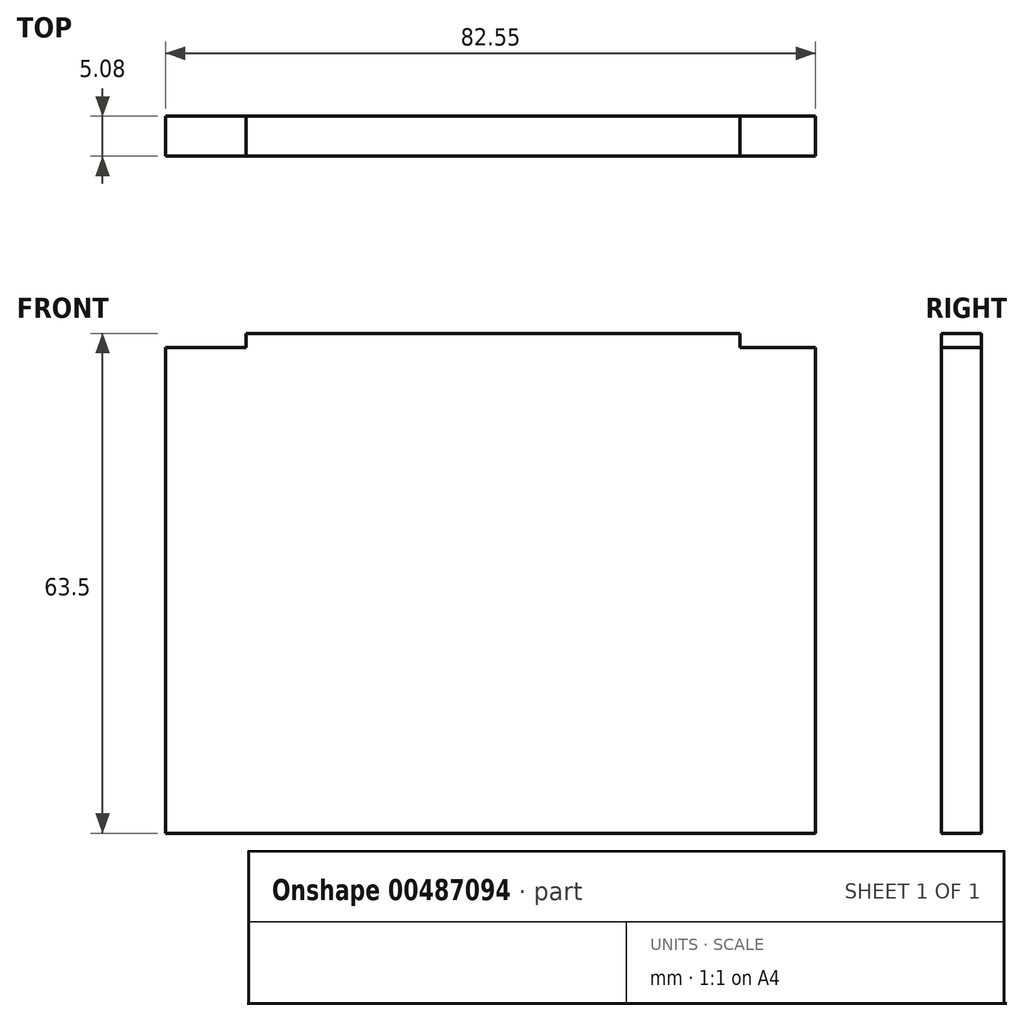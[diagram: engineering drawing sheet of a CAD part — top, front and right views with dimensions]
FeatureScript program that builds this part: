
annotation { "Feature Type Name" : "Feature", "Feature Type Description" : "" }
export const myFeature = defineFeature(function(context is Context, id is Id, definition is map)
    precondition{}
    {
        {
            var Q0;
            Q0=qCreatedBy(makeId("Front.planeOp"),FACE);
            var sketch = newSketch(context, id + "F0", { "sketchPlane" : qUnion([Q0])});
            skLineSegment(sketch, "E0.bottom", {"start": v(-31.37, 30.1) * mm, "end": v(31.37, 30.1) * mm});
            skLineSegment(sketch, "E0.top", {"start": v(-41.58, -33.4) * mm, "end": v(40.97, -33.4) * mm});
            skLineSegment(sketch, "E0.left", {"start": v(-41.58, 28.32) * mm, "end": v(-41.58, -33.4) * mm});
            skLineSegment(sketch, "E0.right", {"start": v(40.97, 28.32) * mm, "end": v(40.97, -33.4) * mm});
            skLineSegment(sketch, "E1.top", {"start": v(31.37, 28.32) * mm, "end": v(40.97, 28.32) * mm});
            skLineSegment(sketch, "E1.left", {"start": v(31.37, 30.1) * mm, "end": v(31.37, 28.32) * mm});
            skLineSegment(sketch, "E2.top", {"start": v(-41.58, 28.32) * mm, "end": v(-31.37, 28.32) * mm});
            skLineSegment(sketch, "E2.right", {"start": v(-31.37, 30.1) * mm, "end": v(-31.37, 28.32) * mm});
            skSolve(sketch);
        }
        {
            var Q0;
            Q0 = qSketchRegion(id + "F0", true);
            extrude(context, id + "F1", {"entities" : qUnion([Q0]), "depth" : 5.08 * mm});
        }
    });
